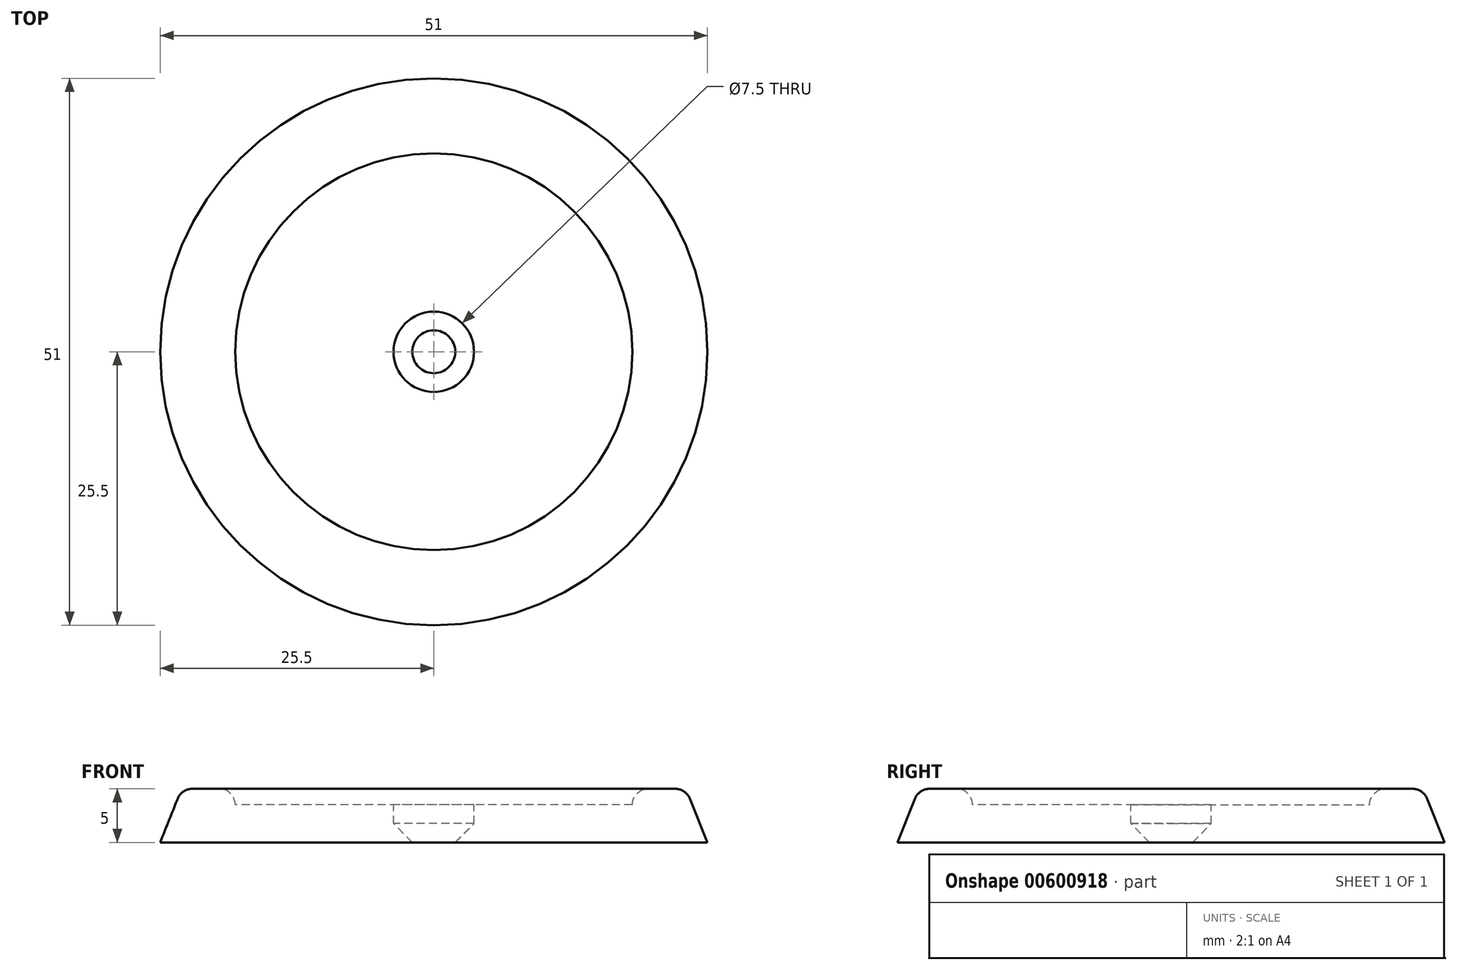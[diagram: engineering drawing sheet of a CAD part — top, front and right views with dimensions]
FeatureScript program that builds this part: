
annotation { "Feature Type Name" : "Feature", "Feature Type Description" : "" }
export const myFeature = defineFeature(function(context is Context, id is Id, definition is map)
    precondition{}
    {
        {
            var Q0;
            Q0=qCreatedBy(makeId("Top.planeOp"),FACE);
            var sketch = newSketch(context, id + "F0", { "sketchPlane" : qUnion([Q0])});
            skCircle(sketch, "E0", {"center": v(0, 0) * mm, "radius": 18.5 * mm});
            skCircle(sketch, "E1", {"center": v(0, 0) * mm, "radius": 2 * mm});
            skSolve(sketch);
        }
        {
            var Q0;
            Q0 = qSketchRegion(id + "F0", true);
            extrude(context, id + "F1", {"entities" : qUnion([Q0]), "depth" : 3.5 * mm, "offsetDistance" : 25 * mm});
        }
        {
            var Q0;
            Q0=makeQuery(id+"F1.opExtrude","CAP_FACE",FACE,{"disambiguationData":[OSD([sQuery(id+"F0.wireOp",EDGE,"E0"),sQuery(id+"F0.wireOp",EDGE,"E1")])],"isStart":false});
            var sketch = newSketch(context, id + "F2", { "sketchPlane" : qUnion([Q0])});
            skCircle(sketch, "E2", {"center": v(0, 0) * mm, "radius": 3.75 * mm});
            skSolve(sketch);
        }
        {
            var Q0;
            Q0 = qSketchRegion(id + "F2", true);
            extrude(context, id + "F3", {"entities" : qUnion([Q0]), "operationType" : NewBodyOperationType.REMOVE, "oppositeDirection" : true, "depth" : .5 * mm, "offsetDistance" : 25 * mm});
        }
        {
            var Q0;
            Q0=makeQuery(id+"F3.boolean.opBoolean","INTERSECT",EDGE,{"derivedFrom":[makeQuery(id+"F1.opExtrude","SWEPT_FACE",FACE,{"disambiguationData":[OSD([sQuery(id+"F0.wireOp",EDGE,"E1")])]}),makeQuery(id+"F3.opExtrude","CAP_FACE",FACE,{"disambiguationData":[OSD([sQuery(id+"F2.wireOp",EDGE,"E2")])],"isStart":false})]});
            chamfer(context, id + "F4", {"entities" : qUnion([Q0]), "width" : 3 * mm, "tangentPropagation" : true});
        }
        {
            var Q0;
            Q0=qCreatedBy(makeId("Right.planeOp"),FACE);
            var sketch = newSketch(context, id + "F5", { "sketchPlane" : qUnion([Q0])});
            skLineSegment(sketch, "E3", {"start": v(0, -33.96) * mm, "end": v(0, 48.14) * mm, "construction": true});
            skSolve(sketch);
        }
        {
            var Q0;
            Q0=qCreatedBy(makeId("Right.planeOp"),FACE);
            var sketch = newSketch(context, id + "F6", { "sketchPlane" : qUnion([Q0])});
            skLineSegment(sketch, "E4", {"start": v(-18.5, 0) * mm, "end": v(-18.5, 5) * mm});
            skLineSegment(sketch, "E5", {"start": v(-18.5, 5) * mm, "end": v(-23.5, 5) * mm});
            skLineSegment(sketch, "E6", {"start": v(-23.5, 5) * mm, "end": v(-25.5, 0) * mm});
            skLineSegment(sketch, "E7", {"start": v(-25.5, 0) * mm, "end": v(-18.5, 0) * mm});
            skLineSegment(sketch, "E8", {"start": v(-18.5, 0) * mm, "end": v(-18.5, 3.5) * mm});
            skSolve(sketch);
        }
        {
            var Q0;
            Q0 = qSketchRegion(id + "F6", true);
            var Q1;
            Q1=sQuery(id+"F5.wireOp",EDGE,"E3");
            revolve(context, id + "F7", {"operationType" : NewBodyOperationType.ADD, "entities" : qUnion([Q0]), "axis" : qUnion([Q1]), "revolveType" : RevolveType.FULL});
        }
        {
            var Q0;
            Q0=makeQuery(id+"F7.opRevolve","SWEPT_EDGE",EDGE,{"disambiguationData":[OSD([sQuery(id+"F6.wireOp",EDGE,"E5"),sQuery(id+"F6.wireOp",EDGE,"E6")])]});
            var Q1;
            Q1=makeQuery(id+"F7.opRevolve","SWEPT_EDGE",EDGE,{"disambiguationData":[OSD([sQuery(id+"F6.wireOp",EDGE,"E4"),sQuery(id+"F6.wireOp",EDGE,"E5")])]});
            fillet(context, id + "F8", {"entities" : qUnion([Q0, Q1]), "radius" : 1.5 * mm, "tangentPropagation" : true, "allowEdgeOverflow" : false});
        }
    });
